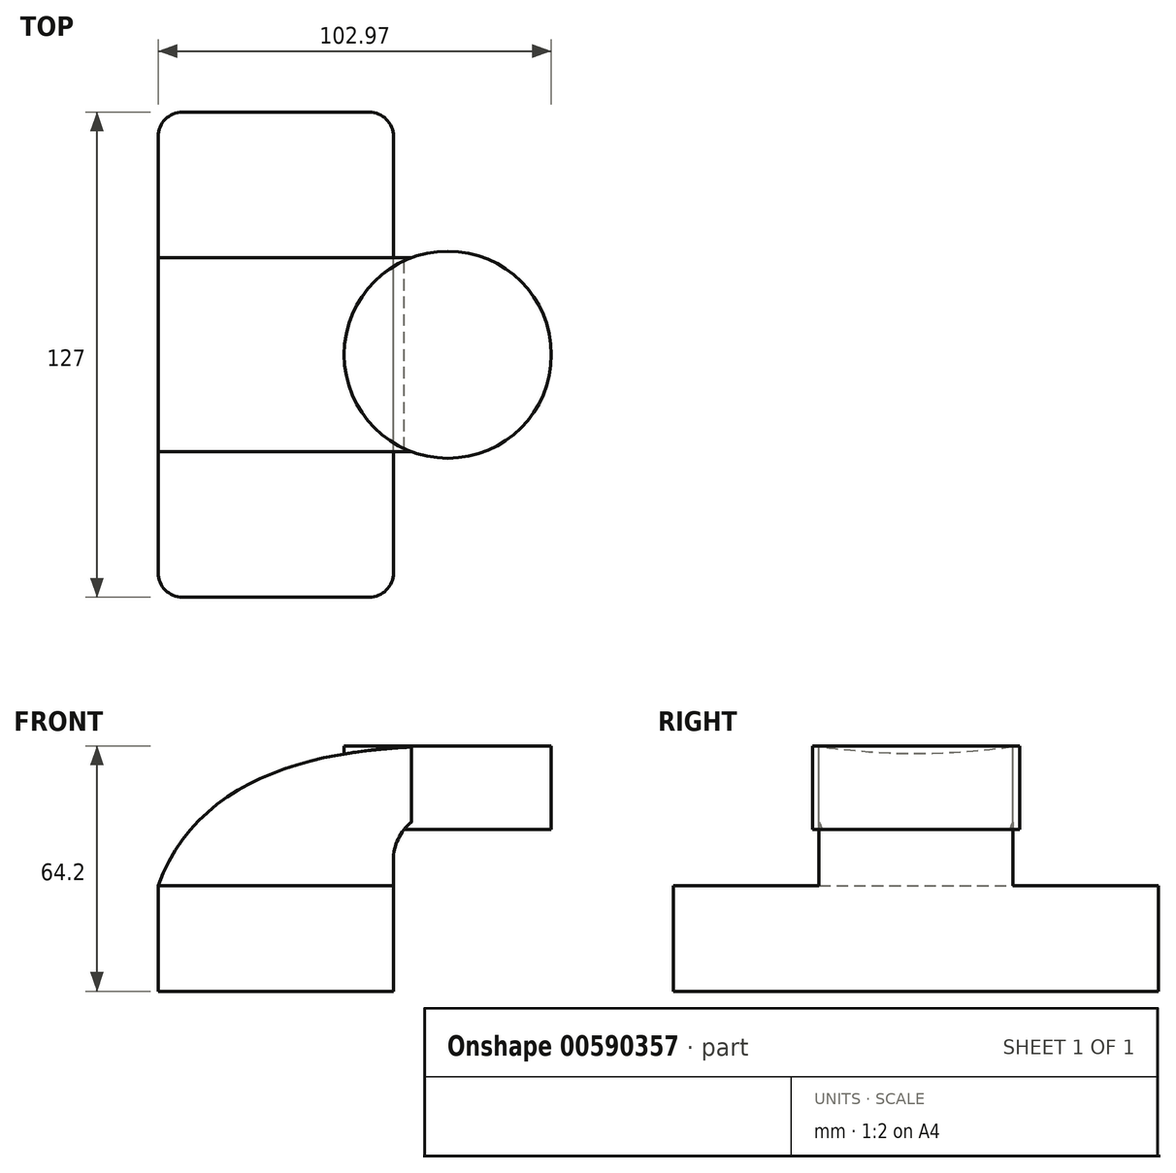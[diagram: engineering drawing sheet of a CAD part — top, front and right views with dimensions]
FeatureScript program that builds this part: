
annotation { "Feature Type Name" : "Feature", "Feature Type Description" : "" }
export const myFeature = defineFeature(function(context is Context, id is Id, definition is map)
    precondition{}
    {
        {
            var Q0;
            Q0=qCreatedBy(makeId("Front.planeOp"),FACE);
            var sketch = newSketch(context, id + "F0", { "sketchPlane" : qUnion([Q0])});
            skLineSegment(sketch, "E0.bottom", {"start": v(-61.62, 21.25) * mm, "end": v(0, 21.25) * mm});
            skLineSegment(sketch, "E0.top", {"start": v(-61.62, -6.33) * mm, "end": v(0, -6.33) * mm});
            skLineSegment(sketch, "E0.left", {"start": v(-61.62, 21.25) * mm, "end": v(-61.62, -6.33) * mm});
            skLineSegment(sketch, "E0.right", {"start": v(0, 21.25) * mm, "end": v(0, -6.33) * mm});
            skLineSegment(sketch, "E1.bottom", {"start": v(14.24, 57.87) * mm, "end": v(41.35, 57.87) * mm});
            skLineSegment(sketch, "E1.top", {"start": v(14.24, 36.1) * mm, "end": v(41.35, 36.1) * mm});
            skLineSegment(sketch, "E1.left", {"start": v(14.24, 57.87) * mm, "end": v(14.24, 36.1) * mm});
            skLineSegment(sketch, "E1.right", {"start": v(41.35, 57.87) * mm, "end": v(41.35, 36.1) * mm});
            skLineSegment(sketch, "E2", {"start": v(0, 21.25) * mm, "end": v(0, 28) * mm});
            skFitSpline(sketch, "E3", {"points": [v(-61.62, 21.25) * mm, v(14.24, 57.87) * mm], "startDerivative": vector(31.53, 86.08) * mm, "endDerivative": vector(104.86, 0.4) * mm});
            skArc(sketch, "E4", {"start": v(0, 28) * mm, "mid": v(4.26, 37.58) * mm, "end": v(14.24, 40.83) * mm});
            skSolve(sketch);
        }
        {
            var Q0;
            Q0=makeQuery(id+"F0.imprint","IMPRINT",FACE,{"disambiguationData":[TD([[makeQuery(id+"F0.imprint","IMPRINT",EDGE,{"derivedFrom":sQuery(id+"F0.wireOp",EDGE,"E0.bottom")}),-1.0]])]});
            extrude(context, id + "F1", {"entities" : qUnion([Q0]), "endBound" : BoundingType.SYMMETRIC, "depth" : 127 * mm, "offsetDistance" : 25.4 * mm});
        }
        {
            var Q0;
            Q0=makeQuery(id+"F0.imprint","IMPRINT",FACE,{"disambiguationData":[TD([[makeQuery(id+"F0.imprint","IMPRINT",EDGE,{"derivedFrom":sQuery(id+"F0.wireOp",EDGE,"E0.bottom")}),1.0]])]});
            extrude(context, id + "F2", {"entities" : qUnion([Q0]), "operationType" : NewBodyOperationType.ADD, "endBound" : BoundingType.SYMMETRIC, "depth" : 50.8 * mm, "offsetDistance" : 25.4 * mm});
        }
        {
            var Q0;
            {var subQ3=sQuery(id+"F0.wireOp",EDGE,"E1.bottom");Q0=makeQuery(id+"F0.imprint","IMPRINT",FACE,{"disambiguationData":[TD([[makeQuery(id+"F0.imprint","IMPRINT",EDGE,{"derivedFrom":subQ3}),-1.0]])]});}
            var Q1;
            Q1=sQuery(id+"F0.wireOp",EDGE,"E1.left");
            revolve(context, id + "F3", {"operationType" : NewBodyOperationType.ADD, "entities" : qUnion([Q0]), "axis" : qUnion([Q1]), "revolveType" : RevolveType.FULL});
        }
        {
            var Q0;
            Q0=makeQuery(id+"F1.opExtrude","CAP_EDGE",EDGE,{"disambiguationData":[OSD([sQuery(id+"F0.wireOp",EDGE,"E0.right")])],"isStart":false});
            var Q1;
            Q1=makeQuery(id+"F1.opExtrude","CAP_EDGE",EDGE,{"disambiguationData":[OSD([sQuery(id+"F0.wireOp",EDGE,"E0.left")])],"isStart":false});
            var Q2;
            Q2=makeQuery(id+"F1.opExtrude","CAP_EDGE",EDGE,{"disambiguationData":[OSD([sQuery(id+"F0.wireOp",EDGE,"E0.right")])],"isStart":true});
            var Q3;
            Q3=makeQuery(id+"F1.opExtrude","CAP_EDGE",EDGE,{"disambiguationData":[OSD([sQuery(id+"F0.wireOp",EDGE,"E0.left")])],"isStart":true});
            fillet(context, id + "F4", {"entities" : qUnion([Q0, Q1, Q2, Q3]), "radius" : 6.35 * mm, "tangentPropagation" : true, "allowEdgeOverflow" : false});
        }
    });
